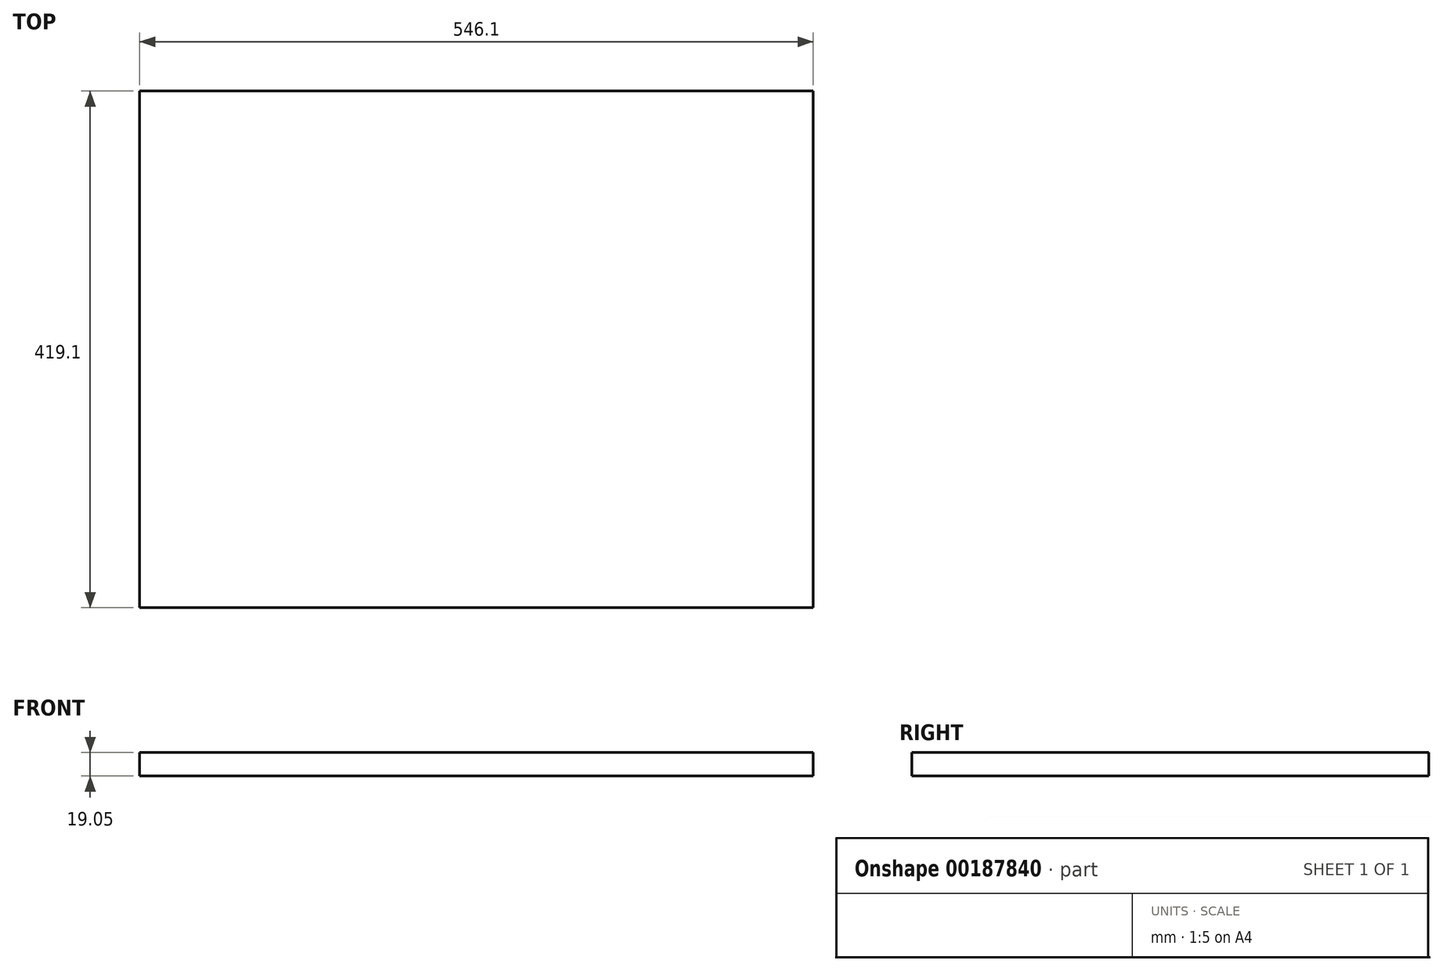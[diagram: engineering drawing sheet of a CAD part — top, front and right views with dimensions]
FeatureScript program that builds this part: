
annotation { "Feature Type Name" : "Feature", "Feature Type Description" : "" }
export const myFeature = defineFeature(function(context is Context, id is Id, definition is map)
    precondition{}
    {
        {
            var Q0;
            Q0=qCreatedBy(makeId("Top.planeOp"),FACE);
            var sketch = newSketch(context, id + "F0", { "sketchPlane" : qUnion([Q0])});
            skLineSegment(sketch, "E0.bottom", {"start": v(273.05, 209.55) * mm, "end": v(-273.05, 209.55) * mm});
            skLineSegment(sketch, "E0.top", {"start": v(273.05, -209.55) * mm, "end": v(-273.05, -209.55) * mm});
            skLineSegment(sketch, "E0.left", {"start": v(273.05, 209.55) * mm, "end": v(273.05, -209.55) * mm});
            skLineSegment(sketch, "E0.right", {"start": v(-273.05, 209.55) * mm, "end": v(-273.05, -209.55) * mm});
            skPoint(sketch, "E0.middle", {"position": v(0, 0) * mm});
            skSolve(sketch);
        }
        {
            var Q0;
            Q0=makeQuery(id+"F0.imprint","IMPRINT",FACE,{"disambiguationData":[TD([[makeQuery(id+"F0.imprint","IMPRINT",EDGE,{"derivedFrom":sQuery(id+"F0.wireOp",EDGE,"E0.bottom")}),1.0]])]});
            extrude(context, id + "F1", {"entities" : qUnion([Q0]), "oppositeDirection" : true, "depth" : 19.05 * mm});
        }
    });
